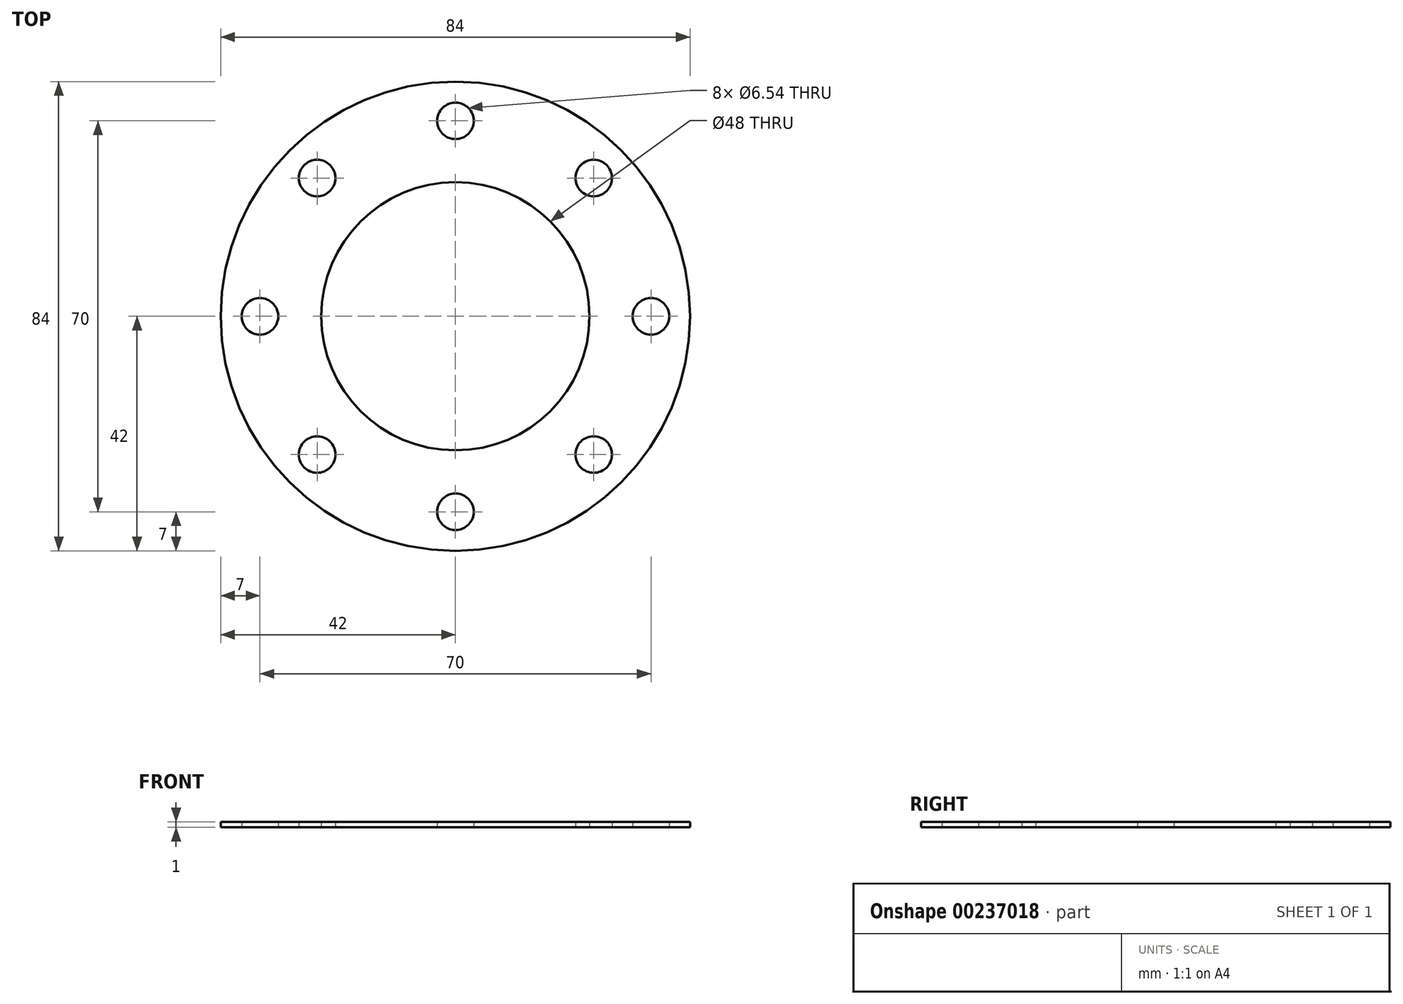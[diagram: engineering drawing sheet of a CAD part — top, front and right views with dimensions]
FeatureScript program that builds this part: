
annotation { "Feature Type Name" : "Feature", "Feature Type Description" : "" }
export const myFeature = defineFeature(function(context is Context, id is Id, definition is map)
    precondition{}
    {
        {
            var Q0;
            Q0=qCreatedBy(makeId("Top.planeOp"),FACE);
            var sketch = newSketch(context, id + "F0", { "sketchPlane" : qUnion([Q0])});
            skCircle(sketch, "E0", {"center": v(0, 0) * mm, "radius": 35 * mm});
            skCircle(sketch, "E1", {"center": v(0, 0) * mm, "radius": 42 * mm});
            skCircle(sketch, "E2", {"center": v(0, 0) * mm, "radius": 24 * mm});
            skCircle(sketch, "E3", {"center": v(0, 35) * mm, "radius": 3.27 * mm});
            skCircle(sketch, "E4.1.0", {"center": v(-24.75, 24.75) * mm, "radius": 3.27 * mm});
            skCircle(sketch, "E4.2.0", {"center": v(-35, 0) * mm, "radius": 3.27 * mm});
            skCircle(sketch, "E4.3.0", {"center": v(-24.75, -24.75) * mm, "radius": 3.27 * mm});
            skCircle(sketch, "E4.4.0", {"center": v(0, -35) * mm, "radius": 3.27 * mm});
            skCircle(sketch, "E4.5.0", {"center": v(24.75, -24.75) * mm, "radius": 3.27 * mm});
            skCircle(sketch, "E4.6.0", {"center": v(35, 0) * mm, "radius": 3.27 * mm});
            skCircle(sketch, "E4.7.0", {"center": v(24.75, 24.75) * mm, "radius": 3.27 * mm});
            skSolve(sketch);
        }
        {
            var Q0;
            Q0=makeQuery(id+"F0.imprint","IMPRINT",FACE,{"disambiguationData":[TD([[makeQuery(id+"F0.imprint","IMPRINT",EDGE,{"derivedFrom":sQuery(id+"F0.wireOp",EDGE,"E1")}),1.0]])]});
            var Q1;
            Q1=makeQuery(id+"F0.imprint","IMPRINT",FACE,{"disambiguationData":[TD([[makeQuery(id+"F0.imprint","IMPRINT",EDGE,{"derivedFrom":sQuery(id+"F0.wireOp",EDGE,"E2")}),-1.0]])]});
            extrude(context, id + "F1", {"entities" : qUnion([Q0, Q1]), "depth" : 1 * mm});
        }
    });
